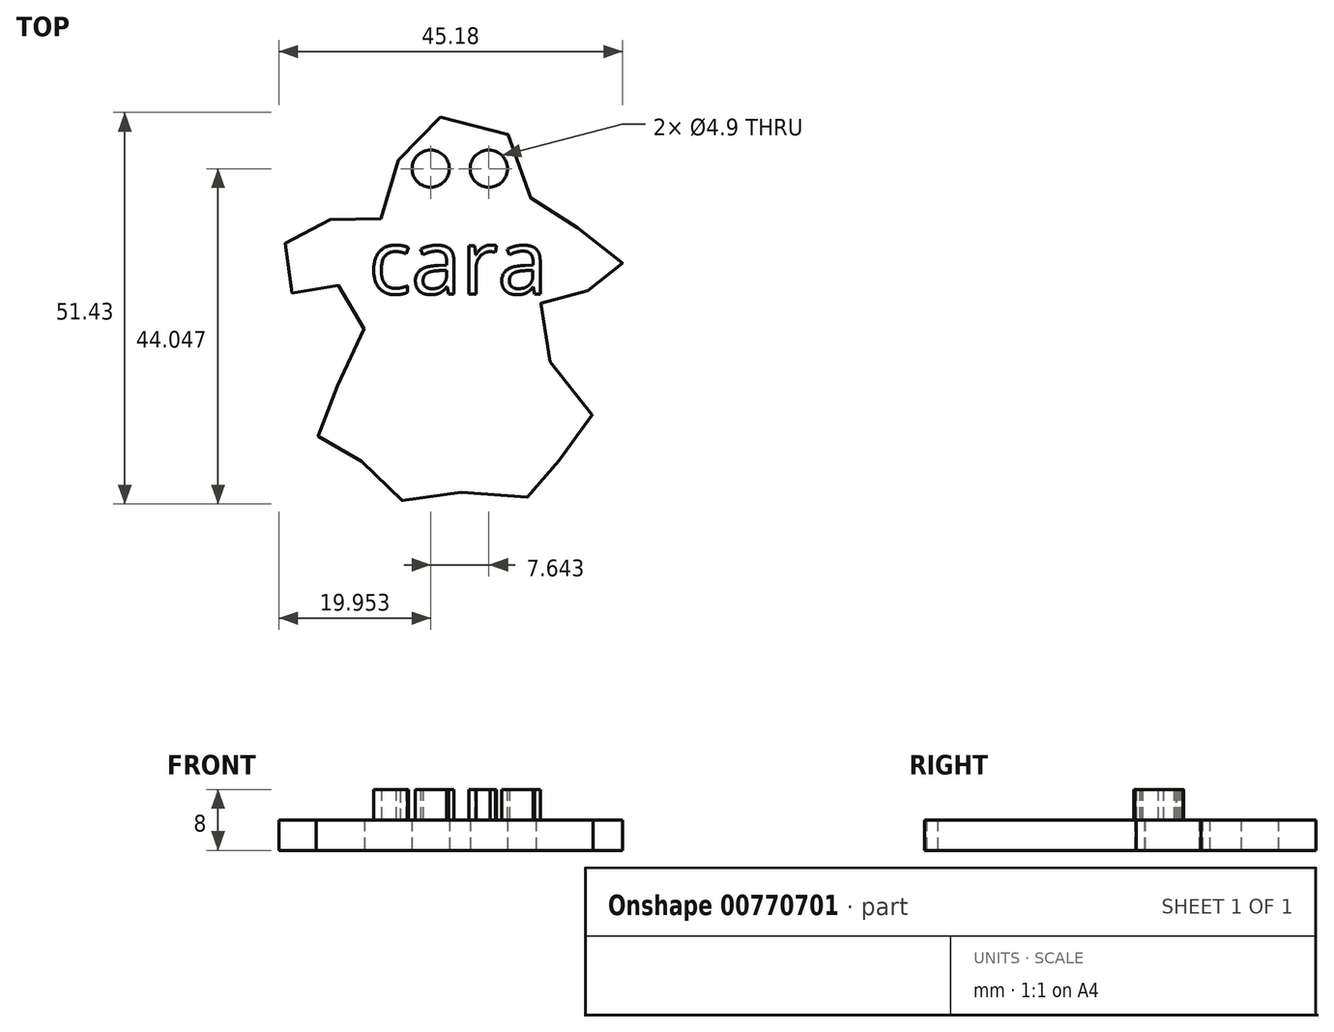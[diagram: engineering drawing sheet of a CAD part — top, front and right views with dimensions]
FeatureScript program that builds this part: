
annotation { "Feature Type Name" : "Feature", "Feature Type Description" : "" }
export const myFeature = defineFeature(function(context is Context, id is Id, definition is map)
    precondition{}
    {
        {
            var Q0;
            Q0=qCreatedBy(makeId("Top.planeOp"),FACE);
            var sketch = newSketch(context, id + "F0", { "sketchPlane" : qUnion([Q0])});
            skFitSpline(sketch, "E0", {"points": [v(-56.23, 62.68) * mm, v(-57.83, 57.88) * mm, v(-59.31, 54.1) * mm, v(-63.54, 54.94) * mm, v(-68, 53.92) * mm, v(-70.64, 52.34) * mm, v(-71.95, 48.5) * mm, v(-70.22, 45.21) * mm, v(-66.86, 46.12) * mm, v(-64.14, 46.22) * mm, v(-61.44, 43.81) * mm, v(-60.84, 39.52) * mm, v(-63.26, 34.18) * mm, v(-66.21, 30.73) * mm, v(-66.82, 26.52) * mm, v(-63.5, 23.92) * mm, v(-60.98, 22.99) * mm, v(-59.09, 19.83) * mm, v(-53.42, 17.76) * mm, v(-48.9, 19.2) * mm, v(-43.25, 17.52) * mm, v(-37.75, 19.73) * mm, v(-36.63, 22.34) * mm, v(-33.23, 24.06) * mm, v(-30.68, 28.53) * mm, v(-33.96, 33.63) * mm, v(-37.65, 38.36) * mm, v(-37.7, 43.45) * mm, v(-34.8, 46.38) * mm, v(-30.64, 45.34) * mm, v(-27.39, 46.54) * mm, v(-27.2, 50.77) * mm, v(-31.14, 53.76) * mm, v(-37.38, 54.02) * mm, v(-39.21, 60.49) * mm, v(-41.48, 65.68) * mm, v(-48.33, 68.93) * mm, v(-53.54, 66.17) * mm, v(-56.23, 62.68) * mm]});
            skCircle(sketch, "E1", {"center": v(-52, 61.55) * mm, "radius": 2.45 * mm});
            skCircle(sketch, "E2", {"center": v(-44.36, 61.55) * mm, "radius": 2.45 * mm});
            skSolve(sketch);
        }
        {
            var Q0;
            Q0 = qSketchRegion(id + "F0", true);
            extrude(context, id + "F1", {"entities" : qUnion([Q0]), "depth" : 4 * mm, "offsetDistance" : 25 * mm});
        }
        {
            var Q0;
            Q0=makeQuery(id+"F1.opExtrude","CAP_FACE",FACE,{"disambiguationData":[OSD([sQuery(id+"F0.wireOp",EDGE,"E0"),sQuery(id+"F0.wireOp",EDGE,"E1"),sQuery(id+"F0.wireOp",EDGE,"E2")])],"isStart":false});
            var sketch = newSketch(context, id + "F2", { "sketchPlane" : qUnion([Q0])});
            skText(sketch, "E3", { "text": "cara", "fontName": "OpenSans-Regular.ttf"});
            const initialGuessF2  = {"E3": [-0.06015, 0.0451, 1, 0, 0.00847]};
            skSetInitialGuess(sketch, initialGuessF2);
            skSolve(sketch);
        }
        {
            var Q0;
            Q0 = qSketchRegion(id + "F2", true);
            extrude(context, id + "F3", {"entities" : qUnion([Q0]), "operationType" : NewBodyOperationType.ADD, "depth" : 4 * mm, "offsetDistance" : 25 * mm});
        }
    });
